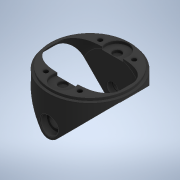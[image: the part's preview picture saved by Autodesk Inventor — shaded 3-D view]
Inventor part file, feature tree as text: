
AUTODESK INVENTOR PART (.ipt)
format: ipt  version: 2020 (Build 240168000, 168)  size: 407,552 bytes
history: native  units: in
note: dims shown in document units (in); Inventor stores cm internally (conversion verified against a paired STEP export)
features: sketch x9, extrude x6, plane x3, revolve x2, hole x2, mirror x1, fillet x1
ambient origin geometry x8: Origin, YZ Plane, XZ Plane, XY Plane, X Axis, Y Axis, Z Axis, Center Point
bodies: Solid1 (feature_tree)
feature tree (24):
  sketch  "Sketch1"  dims[d0=4.0in d1=0.125in]
  revolve  "Revolution1"  [1 undecoded]
  extrude  "Extrusion1"  Depth=0.5in
  mirror  "Mirror1"
  revolve  "Revolution3"  Angle=90.0deg
  plane  "Work Plane1"
  hole  "Hole1"  [1 undecoded]
  extrude  "Extrusion3"  Depth=0.1in
  plane  "Work Plane3"
  extrude  "Extrusion5"  Depth=0.125in
  plane  "Work Plane4"
  extrude  "Extrusion6"  TaperAngle=90.0deg  [1 undecoded]
  extrude  "Extrusion7"  Depth=0.125in
  hole  "Hole2"  [1 undecoded]
  fillet  "Fillet15"  Radius=0.25in
  extrude  "Extrusion8"  Depth=0.125in
  sketch  "Sketch5"  dims[d2=0.5in d3=1.0in]
  sketch  "Sketch6"  dims[d5=1.25in d6=90.0deg]
  sketch  "Sketch7"  dims[d7=0.0938in d8=1.825in d9=0.0in]
  sketch  "Sketch9"  dims[d15=1.75in d16=0.1in]
  sketch  "Sketch11"  dims[d17=0.125in d32=2.0in]
  sketch  "Sketch12"  dims[d33=2.125in d34=90.0deg]
  sketch  "Sketch14"  dims[d37=0.5in]
  sketch  "Sketch15"  dims[d41=0.5in d42=0.75in d43=0.75in d44=0.3125in d45=0.5635in d46=3.0625in d47=0.0in d48=0.375in d49=0.625in d50=0.0in d54=0.25in d55=0.5625in d56=0.25in d57=0.0in d58=0.25in d59=0.0in d64=2.4in d65=1.0in d66=0.125in d67=0.0in d68=2.4in d69=1.5in d70=0.2031in d71=0.75in d72=0.3125in d73=0.875in d74=0.5635in d75=3.0in d76=0.0in d77=0.0312in d79=0.375in d80=0.125in d81=0.0in]
note: 4 required parameter values undecoded (feature->parameter linkage not recoverable at this tier; creation-order binding heuristic only, values carry confidence <= 0.55)